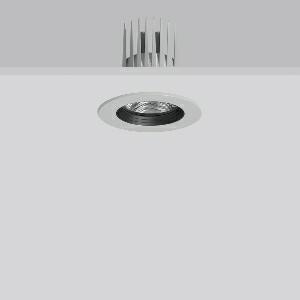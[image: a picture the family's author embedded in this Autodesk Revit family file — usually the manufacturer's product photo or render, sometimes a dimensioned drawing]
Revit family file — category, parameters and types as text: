
# Revit family: heledon_mini_e_901740_004_04d3
name_source: partatom
category: Lighting Fixtures
units: mm (PartAtom-declared; Revit-internal decimal feet)

## family parameters
Cut with Voids When Loaded = No
Host = Face
Light Source = No
Part Type = Normal
Room Calculation Point = No
Round Connector Dimension = Use Diameter
Shared = No

## types (1)
- HELEDON mini E (1 x LED Modul 930, 2500 lm, 3000)
    Apparent Load = 20 VA
    Approval mark = CE
    CIE Flux Codes = 100 100 100 100 100
    Color Rendering = 90
    Color Temperature = 3000
    Default Elevation = 1800 mm
    Description = Series: HELEDON mini
Round recessed downlight. Housing: die-cast aluminium, powder-coated. Black plastic ring and recessed LED to prevent glare from the side. Optical assembly with reflector made of MIRO-Silver with 98% total light reflection for outstanding efficiency - can be changed without tools. Best colour rendering index Ra>90. Suitable for Recessed ceiling mounting. Installation without tools thanks to spring fastening system. Including separate LED converter with connecting cable 600 mm.High quality converter without flickering and stroboscopic effect. Through-wiring box (5 pole) available as accessory. The following accessories can be mounted without use of tools: interchangeable lenses, decorative glasses, honeycomb louvre, clear and frosted diffusers, white interchangeable plastic ring. 
Colour: silver
Diameter: 124 mm
Height: 3 mm
Cut-out diameter: 114 mm
Recess height: 170 mm
Luminaire: recess height: 120 mm
Lamp: LED
Socket: without socket
Colour temperature: 3000K
Colour rendering index (CRI): 92
System power: 20 W
Rated luminous flux: 2500 lm
Luminous efficiency: 125 lm/W
Control gear: Regulated power supply
Protection class: II
Type of protection: IP 20
    Height = 0 mm  [stored 0 ft]
    Lamp = 1 x LED Modul 930
    Lamp Light Flux = 2500 lm
    Lamp count = 1
    Length = 124 mm  [stored 0.406824 ft]
    Lifetime = 50000 h
    Luminous efficacy = 125 lm/W
    Manufacturer = RZB
    ModVariant = No
    Model = 901740.004
    Mounting Place = Ceiling
    Mounting Type = Recessed
    Number of Poles = 1
    OnlyDefault = Yes
    Power Factor = 1
    Product Name = HELEDON mini E
    Product group = Recessed downlights
    ProductGroupID = 402
    Protection Class = Protection class II
    Protection Degree = IP 20
    RLX_Detail_Level = 1
    RLX_Emergency_Light_Flux = 0 lm
    RLX_Emergency_Type = 0
    RLX_Emergency_Type_DB = No
    RlxData = <blob elided: 127529 chars, md5=9f72088e>
    Socket = socket
    Standby Power = 0 W
    System Light Flux = 2500 lm
    System Power = 20 W
    Type Comments = Product without accessories
    Type Image = 901657.004.jpg
    URL = http://relux.com
    VarID = ---
    Voltage = 230 V
    Voltage Range = 220-240 V
    Weight = 0.00 kg
    Width = 0 mm  [stored 0 ft]

note: [stored X ft] marks values corroborated as IEEE doubles in the binary element streams (Revit-internal decimal feet)

## geometry (parser evidence)
native form markers: Blend x4, Sweep x11
no freeform markers — native parametric forms only
